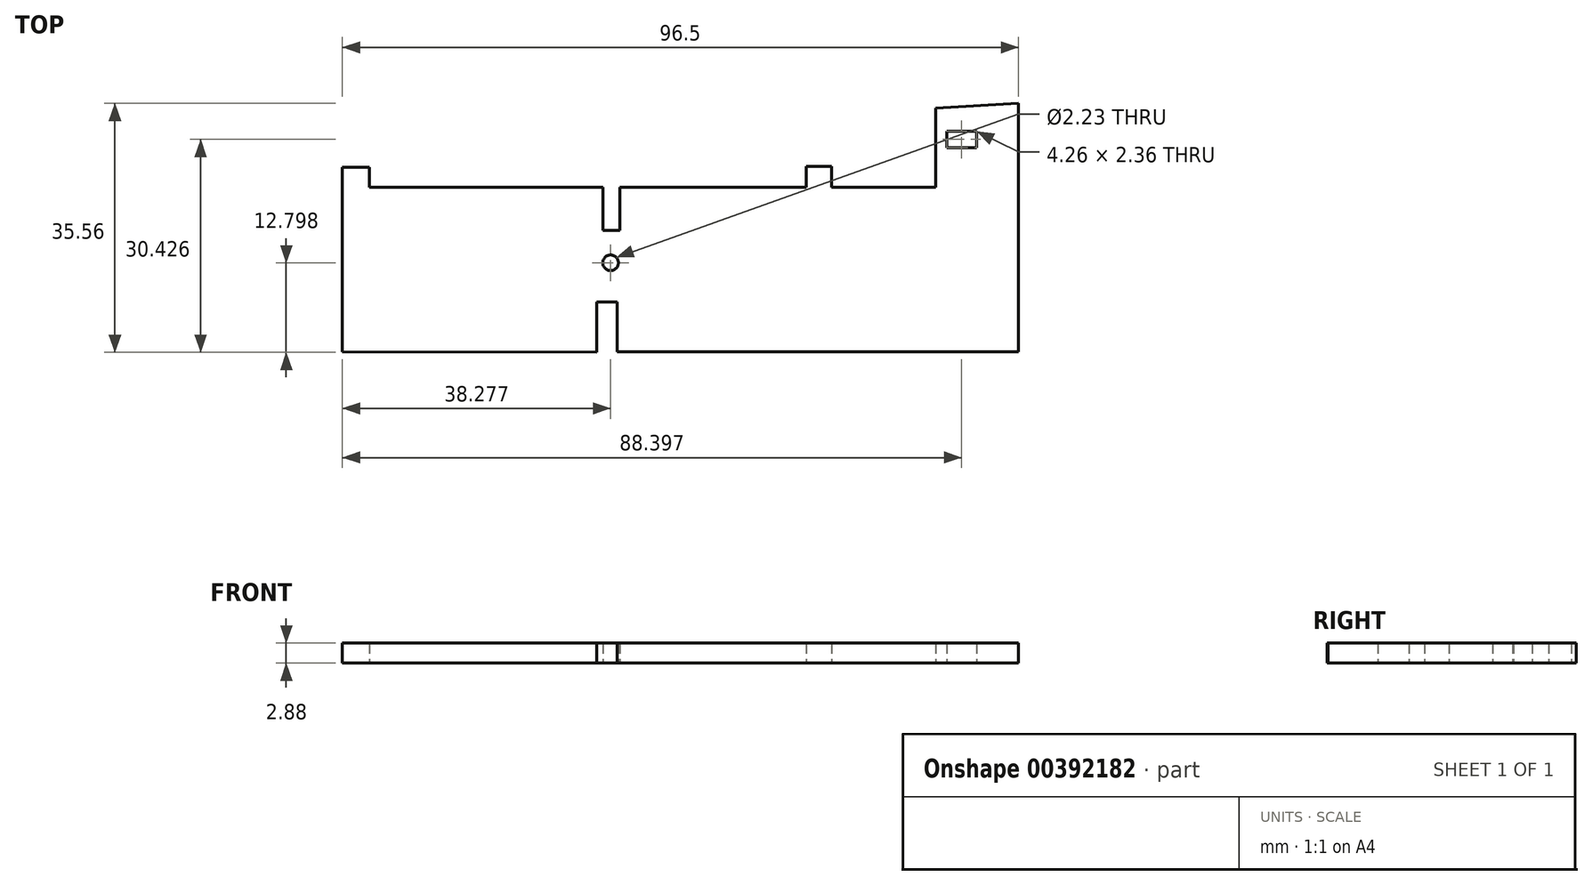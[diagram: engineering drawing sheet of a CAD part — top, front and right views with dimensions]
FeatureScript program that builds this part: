
annotation { "Feature Type Name" : "Feature", "Feature Type Description" : "" }
export const myFeature = defineFeature(function(context is Context, id is Id, definition is map)
    precondition{}
    {
        {
            var Q0;
            Q0=qCreatedBy(makeId("Top.planeOp"),FACE);
            var sketch = newSketch(context, id + "F0", { "sketchPlane" : qUnion([Q0])});
            skLineSegment(sketch, "E0", {"start": v(-35.79, 29.61) * mm, "end": v(-35.79, -5.83) * mm});
            skLineSegment(sketch, "E1", {"start": v(-35.79, -5.83) * mm, "end": v(-93.09, -5.83) * mm});
            skLineSegment(sketch, "E2", {"start": v(-93.09, -5.83) * mm, "end": v(-93.09, 1.27) * mm});
            skLineSegment(sketch, "E3", {"start": v(-93.09, 1.27) * mm, "end": v(-95.97, 1.27) * mm});
            skLineSegment(sketch, "E4", {"start": v(-95.97, 1.27) * mm, "end": v(-95.97, -5.95) * mm});
            skLineSegment(sketch, "E5", {"start": v(-95.97, -5.95) * mm, "end": v(-132.29, -5.83) * mm});
            skLineSegment(sketch, "E6", {"start": v(-132.29, -5.83) * mm, "end": v(-132.29, 20.52) * mm});
            skLineSegment(sketch, "E7", {"start": v(-132.29, 20.52) * mm, "end": v(-128.47, 20.52) * mm});
            skLineSegment(sketch, "E8", {"start": v(-128.47, 20.52) * mm, "end": v(-128.47, 17.66) * mm});
            skLineSegment(sketch, "E9", {"start": v(-128.47, 17.66) * mm, "end": v(-95.09, 17.66) * mm});
            skLineSegment(sketch, "E10", {"start": v(-95.09, 17.66) * mm, "end": v(-95.09, 11.46) * mm});
            skLineSegment(sketch, "E11", {"start": v(-95.09, 11.46) * mm, "end": v(-92.7, 11.46) * mm});
            skLineSegment(sketch, "E12", {"start": v(-92.7, 11.46) * mm, "end": v(-92.7, 17.66) * mm});
            skLineSegment(sketch, "E13", {"start": v(-92.7, 17.66) * mm, "end": v(-66.1, 17.66) * mm});
            skLineSegment(sketch, "E14", {"start": v(-66.1, 17.66) * mm, "end": v(-66.1, 20.63) * mm});
            skLineSegment(sketch, "E15", {"start": v(-66.1, 20.63) * mm, "end": v(-62.44, 20.63) * mm});
            skLineSegment(sketch, "E16", {"start": v(-62.44, 20.63) * mm, "end": v(-62.44, 17.66) * mm});
            skLineSegment(sketch, "E17", {"start": v(-62.44, 17.66) * mm, "end": v(-47.6, 17.66) * mm});
            skLineSegment(sketch, "E18", {"start": v(-47.6, 17.66) * mm, "end": v(-47.6, 28.93) * mm});
            skLineSegment(sketch, "E19", {"start": v(-47.6, 28.93) * mm, "end": v(-35.79, 29.61) * mm});
            skPoint(sketch, "E20.firstSnap0", {"position": v(-47.6, 23.3) * mm});
            skLineSegment(sketch, "E20.bottom", {"start": v(-46.02, 23.3) * mm, "end": v(-41.76, 23.3) * mm});
            skLineSegment(sketch, "E20.top", {"start": v(-46.02, 25.66) * mm, "end": v(-41.76, 25.66) * mm});
            skLineSegment(sketch, "E20.left", {"start": v(-46.02, 23.3) * mm, "end": v(-46.02, 25.66) * mm});
            skLineSegment(sketch, "E20.right", {"start": v(-41.76, 23.3) * mm, "end": v(-41.76, 25.66) * mm});
            skCircle(sketch, "E21", {"center": v(-94.01, 6.85) * mm, "radius": 1.12 * mm});
            skSolve(sketch);
        }
        {
            var Q0;
            Q0 = qSketchRegion(id + "F0", true);
            extrude(context, id + "F1", {"entities" : qUnion([Q0]), "depth" : 2.88 * mm});
        }
    });
